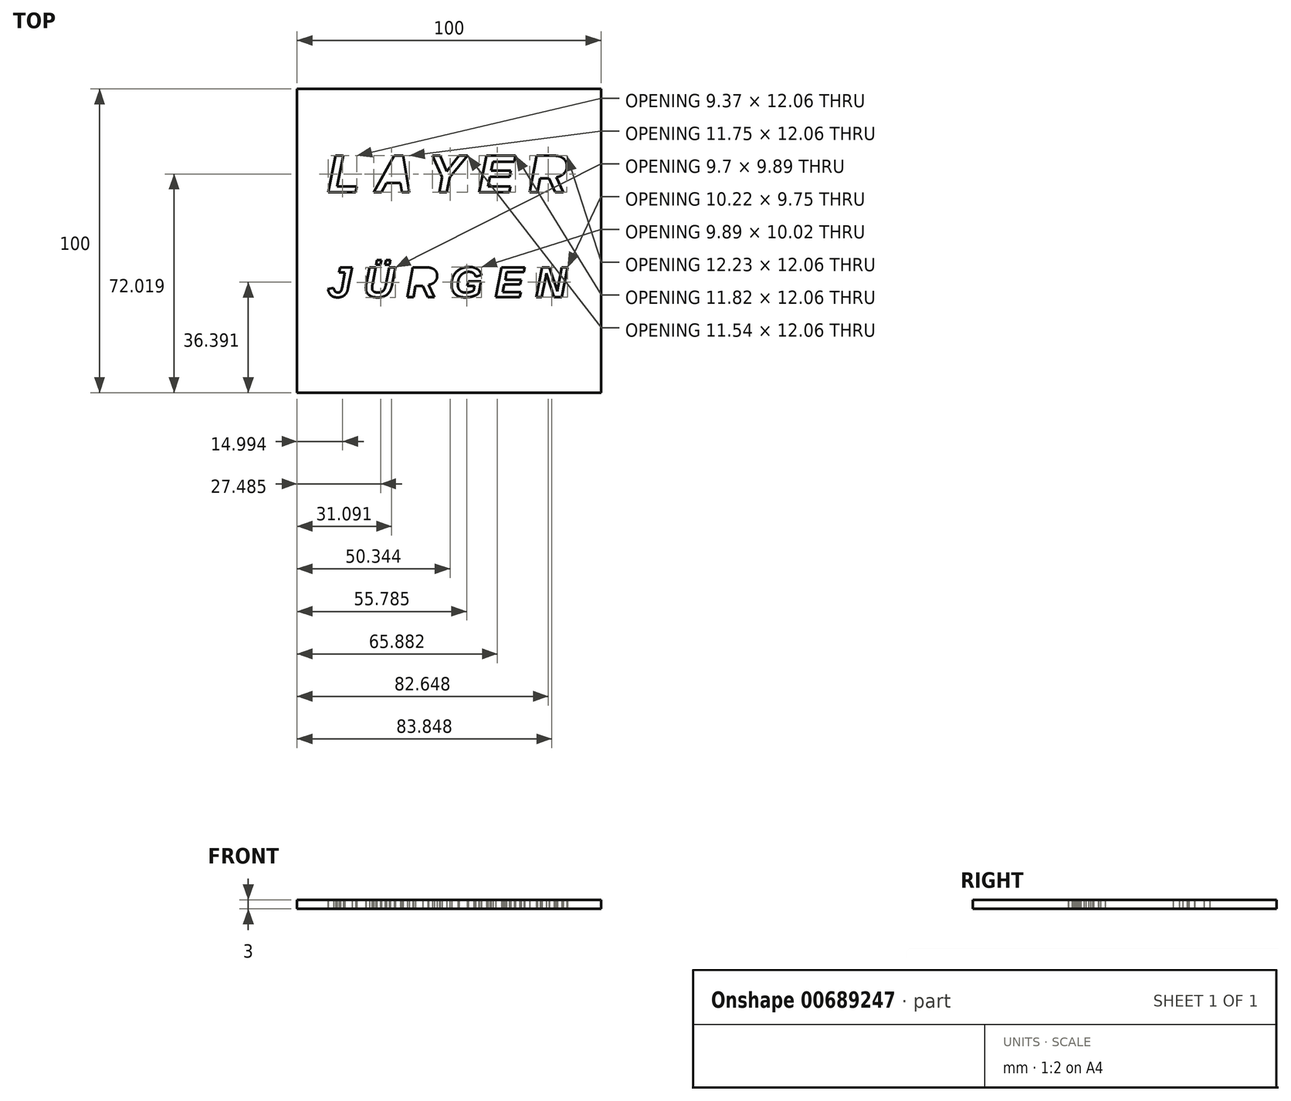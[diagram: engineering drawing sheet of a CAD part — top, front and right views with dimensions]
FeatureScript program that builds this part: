
annotation { "Feature Type Name" : "Feature", "Feature Type Description" : "" }
export const myFeature = defineFeature(function(context is Context, id is Id, definition is map)
    precondition{}
    {
        {
            var Q0;
            Q0=qCreatedBy(makeId("Top.planeOp"),FACE);
            var sketch = newSketch(context, id + "F0", { "sketchPlane" : qUnion([Q0])});
            skLineSegment(sketch, "E0.bottom", {"start": v(-50, 29.58) * mm, "end": v(50, 29.58) * mm});
            skLineSegment(sketch, "E0.top", {"start": v(-50, -70.42) * mm, "end": v(50, -70.42) * mm});
            skLineSegment(sketch, "E0.left", {"start": v(-50, 29.58) * mm, "end": v(-50, -70.42) * mm});
            skLineSegment(sketch, "E0.right", {"start": v(50, 29.58) * mm, "end": v(50, -70.42) * mm});
            skText(sketch, "E1", { "text": "L A Y E R", "fontName": "Arimo-BoldItalic.ttf"});
            skText(sketch, "E2", { "text": "J Ü R G E N", "fontName": "Arimo-BoldItalic.ttf"});
            const initialGuessF0  = {"E1": [-0.04, -0.00443, 1, 0, 0.01262], "E2": [-0.04, -0.03891, 1, 0, 0.0102]};
            skSetInitialGuess(sketch, initialGuessF0);
            skSolve(sketch);
        }
        {
            var Q0;
            Q0 = qSketchRegion(id + "F0", true);
            extrude(context, id + "F1", {"entities" : qUnion([Q0]), "depth" : 3 * mm, "offsetDistance" : 25 * mm});
        }
    });
